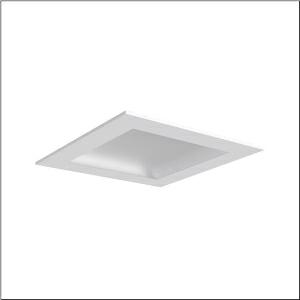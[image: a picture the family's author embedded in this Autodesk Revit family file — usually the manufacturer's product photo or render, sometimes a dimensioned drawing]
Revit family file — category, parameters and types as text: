
# Revit family: mira_11_sl_51fr427a443a
name_source: partatom
category: Lighting Fixtures
units: mm (PartAtom-declared; Revit-internal decimal feet)

## family parameters
Cut with Voids When Loaded = No
Host = Face
Light Source = No
Part Type = Normal
Room Calculation Point = No
Round Connector Dimension = Use Diameter
Shared = No

## types (1)
- Mira 11 SL (1 x LED, 4430 lm, 40 W, 4000K)
    Apparent Load = 40 VA
    CIE Flux Codes = 50 81 97 100 100
    Color Rendering = 80
    Color Temperature = 4000K
    Default Elevation = 1800 mm
    Description = Mira 11 SL, clean room luminaire, primary light control with reflector, primary optical cover: cover, of PC, light emission: direct distribution, primary light characteristic: symmetric, installation type: recessed, LED, rated luminous flux: 4.430lm, luminous efficacy: 111lm/W, light colour: 840, colour temperature: 4000K, control gear: ON/OFF, with terminal, 3-pole, max. 2.5mm², mains connection: 230V, AC, 50/60Hz, rated input power: 40W, luminaire housing, of sheet steel, coated, pure white (RAL 9010), with wing nuts, module: M625, length: 623mm, width: 623mm, height: 91mm, protection rating (complete): IP54, protection rating (on room side): IP65, insulation class (complete): insulation class I (protective earthing), certification: CE, UKCA, permissible operating ambient temperature: -5..+40°C, standard: EN 50419, packaging unit: 1 piece
    Height = 0 mm  [stored 0 ft]
    Lamp = 1 x LED
    Lamp Light Flux = 4430 lm
    Lamp Power = 40 W
    Lamp count = 1
    Length = 625 mm
    Luminous efficacy = 111 lm/W
    Manufacturer = Siteco
    ModVariant = No
    Model = 51FR427A443A
    Mounting Place = Ceiling
    Mounting Type = Recessed
    Number of Poles = 1
    OnlyDefault = Yes
    Power Factor = 1
    Product Name = Mira 11 SL
    Product group = clean room luminaire | ceiling recessed
    ProductGroupID = 402
    Protection Class = Protection class I
    Protection Degree = IP 54
    RLX_Detail_Level = 1
    RLX_Emergency_Light_Flux = 0 lm
    RLX_Emergency_Type = 0
    RLX_Emergency_Type_DB = No
    RlxData = <blob elided: 19933 chars, md5=52bfd927>
    Socket = socket
    Standby Power = 0 W
    System Light Flux = 4430 lm
    System Power = 40 W
    Type Comments = Product without accessories
    Type Image = l_1007111.jpg
    URL = http://relux.com
    VarID = ---
    Voltage = 0 V
    Weight = 0.00 kg
    Width = 625 mm

note: [stored X ft] marks values corroborated as IEEE doubles in the binary element streams (Revit-internal decimal feet)

## geometry (parser evidence)
native form markers: Blend x4, Sweep x12
no freeform markers — native parametric forms only
